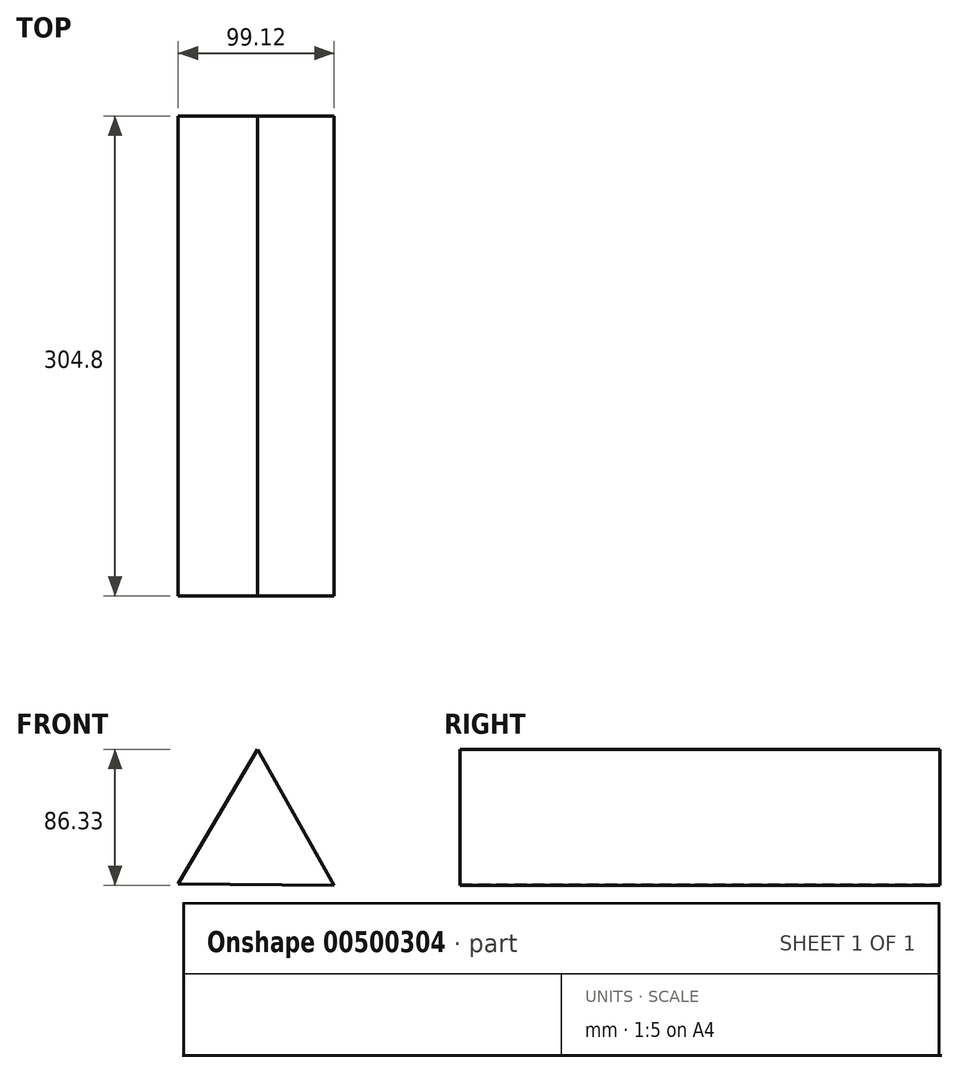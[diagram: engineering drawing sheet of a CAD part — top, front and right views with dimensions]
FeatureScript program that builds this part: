
annotation { "Feature Type Name" : "Feature", "Feature Type Description" : "" }
export const myFeature = defineFeature(function(context is Context, id is Id, definition is map)
    precondition{}
    {
        {
            var Q0;
            Q0=qCreatedBy(makeId("Front.planeOp"),FACE);
            var sketch = newSketch(context, id + "F0", { "sketchPlane" : qUnion([Q0])});
            skCircle(sketch, "E0.cCircle", {"center": v(0, 0) * mm, "radius": 57.23 * mm, "construction": true});
            skLineSegment(sketch, "E0.0", {"start": v(0.56, 57.23) * mm, "end": v(49.28, -29.1) * mm});
            skLineSegment(sketch, "E0.1", {"start": v(49.28, -29.1) * mm, "end": v(-49.84, -28.13) * mm});
            skLineSegment(sketch, "E0.2", {"start": v(-49.84, -28.13) * mm, "end": v(0.56, 57.23) * mm});
            skSolve(sketch);
        }
        {
            var Q0;
            Q0=makeQuery(id+"F0.imprint","IMPRINT",FACE,{"disambiguationData":[TD([[makeQuery(id+"F0.imprint","IMPRINT",EDGE,{"derivedFrom":sQuery(id+"F0.wireOp",EDGE,"E0.0")}),-1.0]])]});
            extrude(context, id + "F1", {"entities" : qUnion([Q0]), "depth" : 304.8 * mm});
        }
    });
